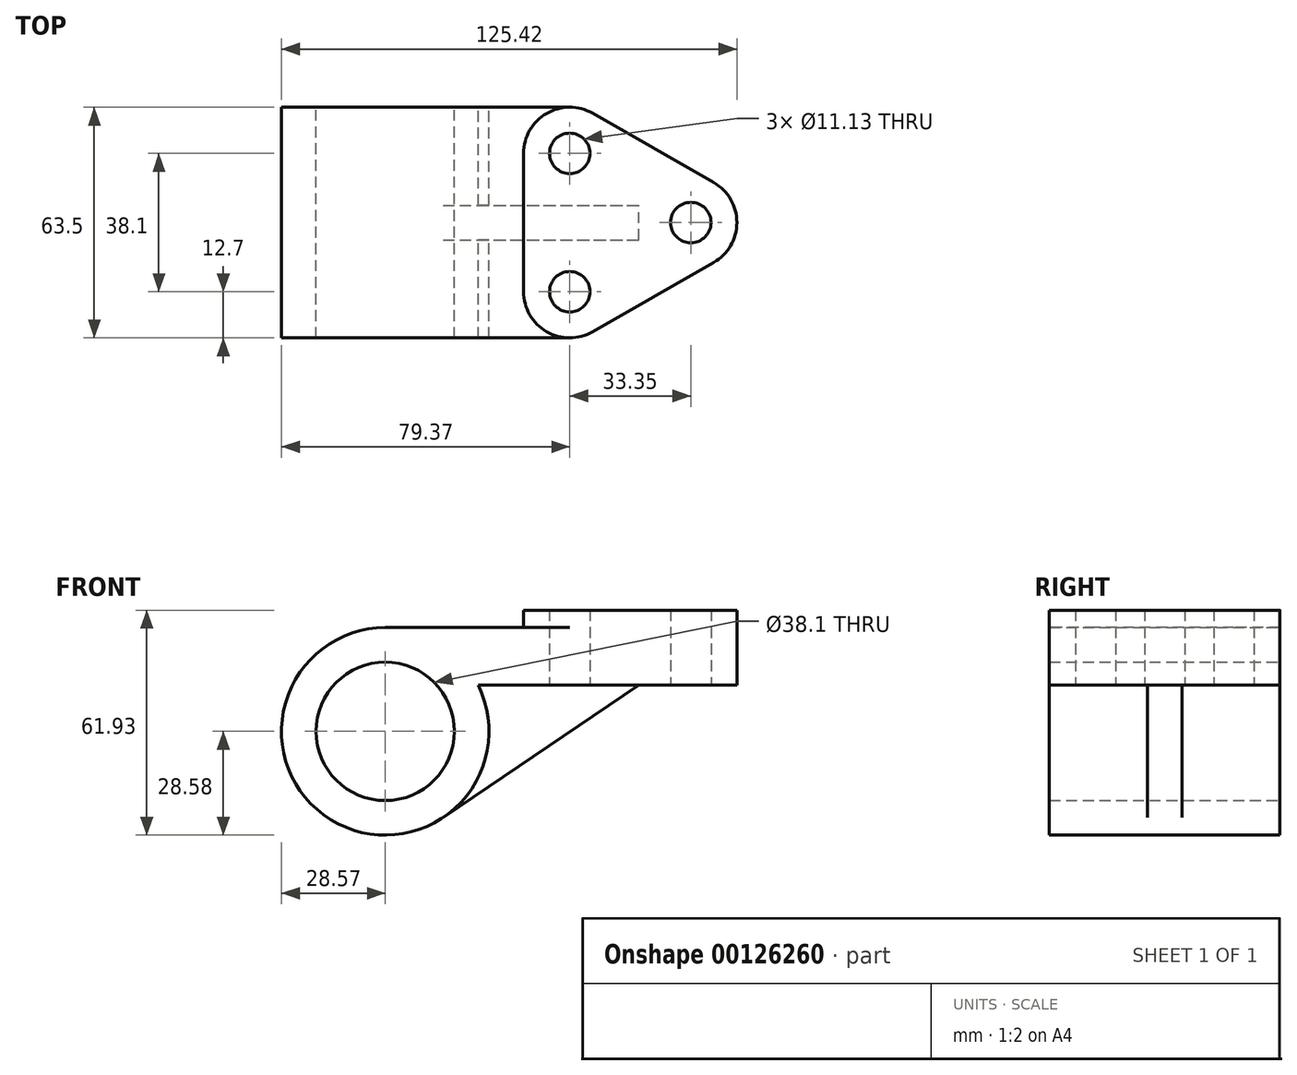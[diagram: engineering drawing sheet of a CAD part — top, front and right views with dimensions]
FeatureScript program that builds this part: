
annotation { "Feature Type Name" : "Feature", "Feature Type Description" : "" }
export const myFeature = defineFeature(function(context is Context, id is Id, definition is map)
    precondition{}
    {
        {
            var Q0;
            Q0=qCreatedBy(makeId("Front.planeOp"),FACE);
            var sketch = newSketch(context, id + "F0", { "sketchPlane" : qUnion([Q0])});
            skCircle(sketch, "E0", {"center": v(0, 0) * mm, "radius": 19.05 * mm});
            skLineSegment(sketch, "E1", {"start": v(0, 28.58) * mm, "end": v(50.8, 28.58) * mm});
            skArc(sketch, "E2", {"start": v(0, 28.58) * mm, "mid": v(-15.06, -24.28) * mm, "end": v(25.6, 12.7) * mm});
            skLineSegment(sketch, "E3", {"start": v(25.6, 12.7) * mm, "end": v(50.8, 12.7) * mm});
            skLineSegment(sketch, "E4", {"start": v(50.8, 28.58) * mm, "end": v(50.8, 12.7) * mm});
            skSolve(sketch);
        }
        {
            var Q0;
            Q0 = qSketchRegion(id + "F0", true);
            extrude(context, id + "F1", {"entities" : qUnion([Q0]), "endBound" : BoundingType.SYMMETRIC, "depth" : 63.5 * mm});
        }
        {
            var Q0;
            Q0=makeQuery(id+"F1.opExtrude","SWEPT_FACE",FACE,{"disambiguationData":[OSD([sQuery(id+"F0.wireOp",EDGE,"E3")])]});
            var sketch = newSketch(context, id + "F2", { "sketchPlane" : qUnion([Q0])});
            skLineSegment(sketch, "E5", {"start": v(57.1, 30.08) * mm, "end": v(90.45, 11.03) * mm});
            skLineSegment(sketch, "E6", {"start": v(57.1, -30.08) * mm, "end": v(90.45, -11.03) * mm});
            skArc(sketch, "E7", {"start": v(90.45, -11.03) * mm, "mid": v(96.85, 0) * mm, "end": v(90.45, 11.03) * mm});
            skLineSegment(sketch, "E8", {"start": v(38.1, 19.05) * mm, "end": v(38.1, -19.05) * mm});
            skArc(sketch, "E9", {"start": v(38.1, -19.05) * mm, "mid": v(44.42, -30.03) * mm, "end": v(57.1, -30.08) * mm});
            skArc(sketch, "E10", {"start": v(57.1, 30.08) * mm, "mid": v(44.42, 30.03) * mm, "end": v(38.1, 19.05) * mm});
            skCircle(sketch, "E11", {"center": v(50.8, 19.05) * mm, "radius": 5.56 * mm});
            skCircle(sketch, "E12", {"center": v(50.8, -19.05) * mm, "radius": 5.56 * mm});
            skCircle(sketch, "E13", {"center": v(84.15, 0) * mm, "radius": 5.56 * mm});
            skSolve(sketch);
        }
        {
            var Q0;
            {var subQ4=sQuery(id+"F2.wireOp",EDGE,"E8");Q0=makeQuery(id+"F2.imprint","IMPRINT",FACE,{"disambiguationData":[TD([[makeQuery(id+"F2.imprint","IMPRINT",EDGE,{"derivedFrom":subQ4}),1.0]])]});}
            var Q1;
            {var subQ11=sQuery(id+"F2.wireOp",EDGE,"E5");Q1=makeQuery(id+"F2.imprint","IMPRINT",FACE,{"disambiguationData":[TD([[makeQuery(id+"F2.imprint","IMPRINT",EDGE,{"derivedFrom":subQ11}),-1.0]])]});}
            extrude(context, id + "F3", {"entities" : qUnion([Q0, Q1]), "operationType" : NewBodyOperationType.ADD, "oppositeDirection" : true, "depth" : 20.65 * mm});
        }
        {
            var Q0;
            Q0=makeQuery(id+"F3.boolean.opBoolean","SPLIT",FACE,{"disambiguationData":[TD([makeQuery(id+"F3.opExtrude","SWEPT_FACE",FACE,{"disambiguationData":[OSD([sQuery(id+"F2.wireOp",EDGE,"E12")])]})])],"derivedFrom":makeQuery(id+"F1.opExtrude","SWEPT_FACE",FACE,{"disambiguationData":[OSD([sQuery(id+"F0.wireOp",EDGE,"E1")])]})});
            var Q1;
            Q1=makeQuery(id+"F3.boolean.opBoolean","SPLIT",FACE,{"disambiguationData":[TD([makeQuery(id+"F3.opExtrude","SWEPT_FACE",FACE,{"disambiguationData":[OSD([sQuery(id+"F2.wireOp",EDGE,"E11")])]})])],"derivedFrom":makeQuery(id+"F1.opExtrude","SWEPT_FACE",FACE,{"disambiguationData":[OSD([sQuery(id+"F0.wireOp",EDGE,"E1")])]})});
            extrude(context, id + "F4", {"entities" : qUnion([Q0, Q1]), "operationType" : NewBodyOperationType.REMOVE, "endBound" : BoundingType.THROUGH_ALL, "oppositeDirection" : true, "depth" : 25.4 * mm});
        }
        {
            var Q0;
            Q0=qCreatedBy(makeId("Front.planeOp"),FACE);
            var sketch = newSketch(context, id + "F5", { "sketchPlane" : qUnion([Q0])});
            skLineSegment(sketch, "E14", {"start": v(16, -23.68) * mm, "end": v(69.85, 12.7) * mm});
            skArc(sketch, "E15", {"start": v(25.6, 12.7) * mm, "mid": v(27.63, -7.3) * mm, "end": v(16, -23.68) * mm});
            skLineSegment(sketch, "E16", {"start": v(25.6, 12.7) * mm, "end": v(69.85, 12.7) * mm});
            skSolve(sketch);
        }
        {
            var Q0;
            Q0 = qSketchRegion(id + "F5", true);
            var Q1;
            Q1=makeQuery(id+"F5.imprint","IMPRINT",FACE,{"disambiguationData":[TD([[makeQuery(id+"F5.imprint","IMPRINT",EDGE,{"derivedFrom":sQuery(id+"F5.wireOp",EDGE,"E14")}),1.0]])]});
            extrude(context, id + "F6", {"entities" : qUnion([Q0, Q1]), "operationType" : NewBodyOperationType.ADD, "endBound" : BoundingType.SYMMETRIC, "depth" : 9.52 * mm});
        }
    });
